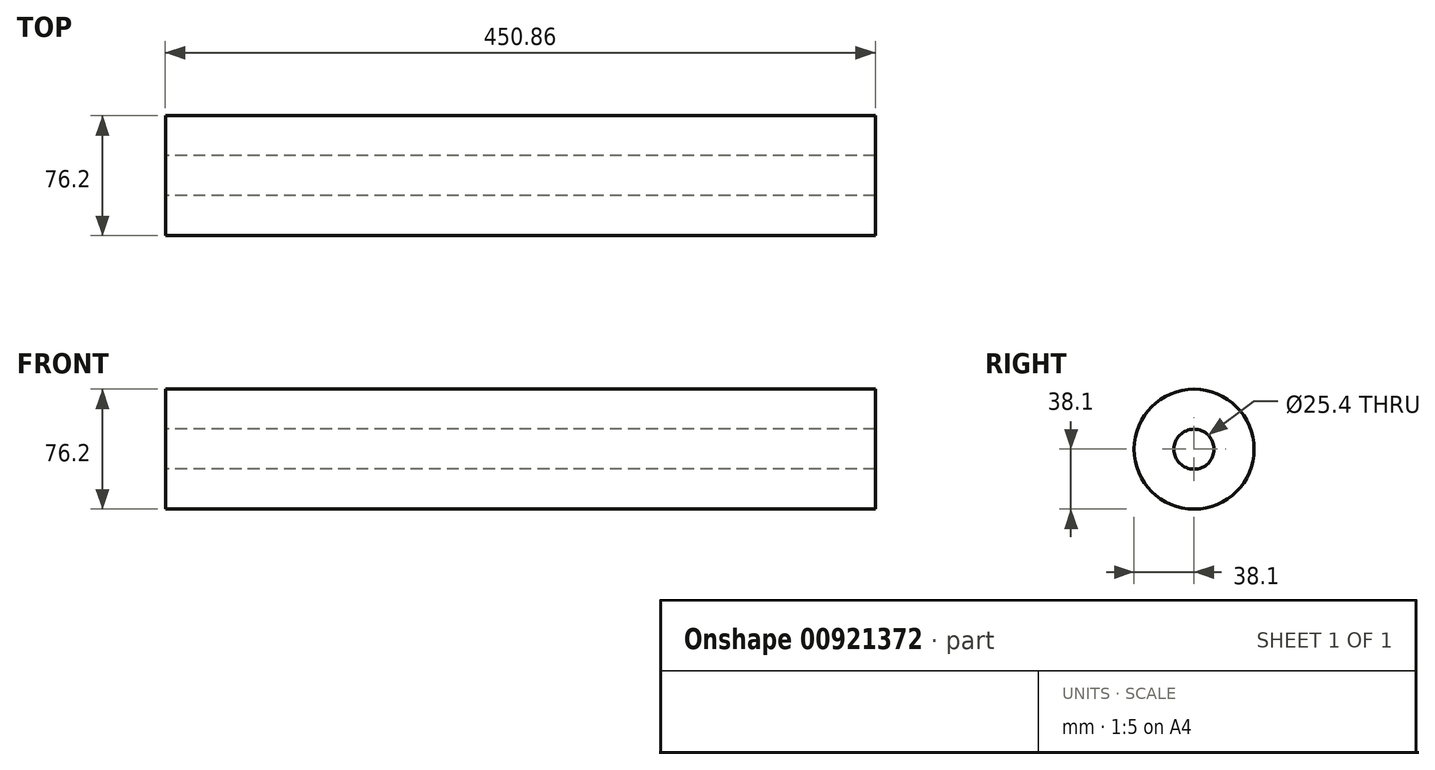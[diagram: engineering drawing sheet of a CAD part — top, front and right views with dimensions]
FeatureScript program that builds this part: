
annotation { "Feature Type Name" : "Feature", "Feature Type Description" : "" }
export const myFeature = defineFeature(function(context is Context, id is Id, definition is map)
    precondition{}
    {
        {
            var Q0;
            Q0=qCreatedBy(makeId("Right.planeOp"),FACE);
            var sketch = newSketch(context, id + "F0", { "sketchPlane" : qUnion([Q0])});
            skCircle(sketch, "E0", {"center": v(0, 0) * mm, "radius": 12.7 * mm});
            skCircle(sketch, "E1", {"center": v(0, 0) * mm, "radius": 38.1 * mm});
            skSolve(sketch);
        }
        {
            var Q0;
            Q0 = qSketchRegion(id + "F0", true);
            extrude(context, id + "F1", {"entities" : qUnion([Q0]), "endBound" : BoundingType.SYMMETRIC, "depth" : 450.85 * mm, "offsetDistance" : 25.4 * mm});
        }
    });
